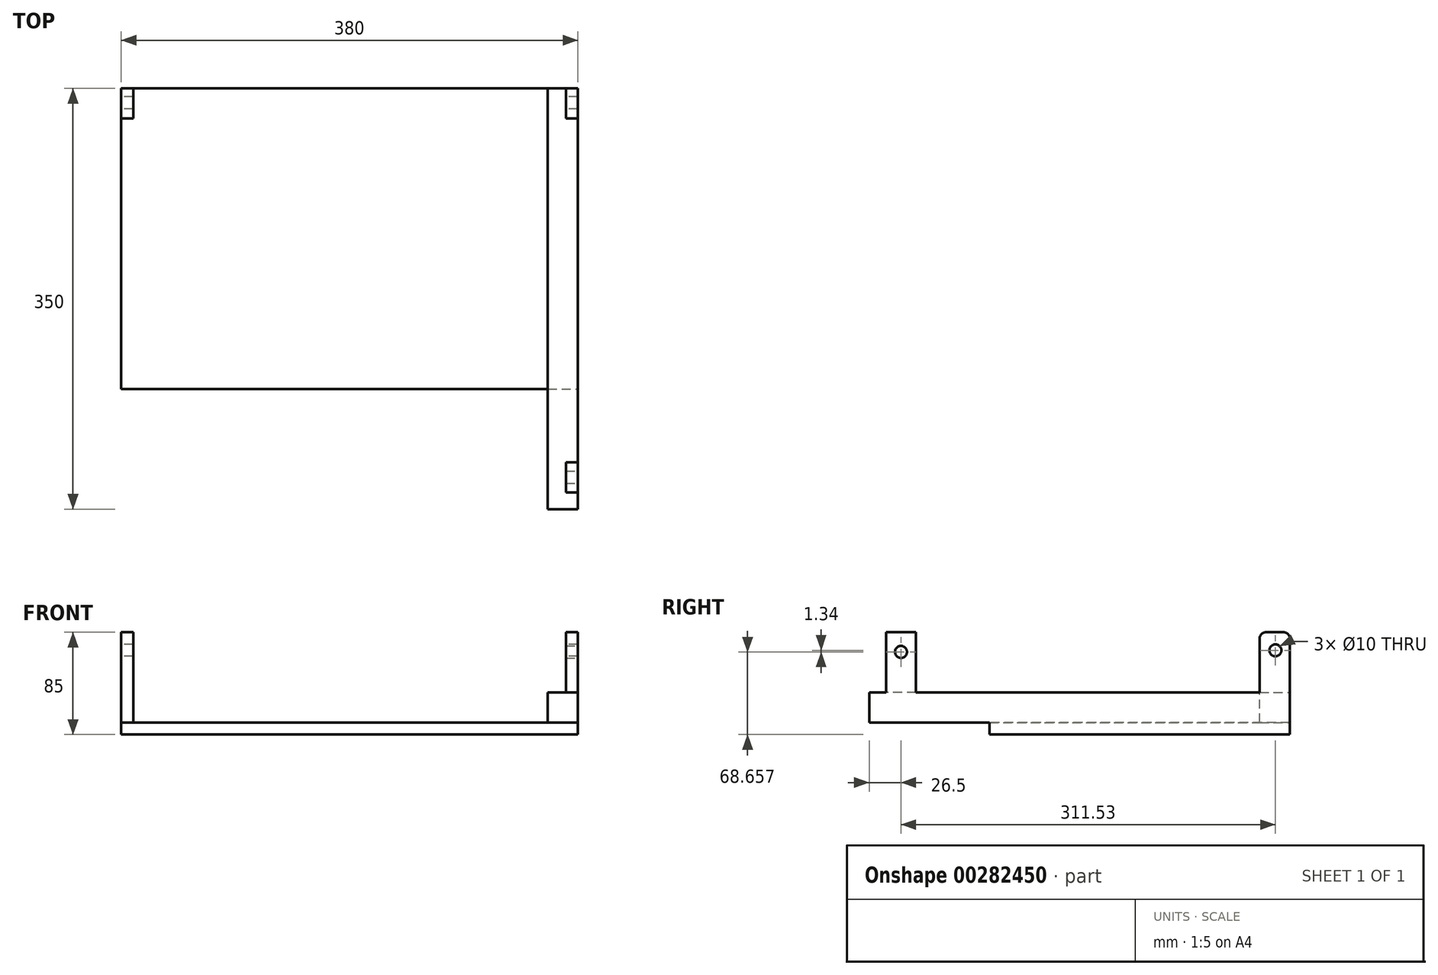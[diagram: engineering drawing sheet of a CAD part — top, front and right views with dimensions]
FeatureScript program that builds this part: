
annotation { "Feature Type Name" : "Feature", "Feature Type Description" : "" }
export const myFeature = defineFeature(function(context is Context, id is Id, definition is map)
    precondition{}
    {
        {
            var Q0;
            Q0=qCreatedBy(makeId("Front.planeOp"),FACE);
            var sketch = newSketch(context, id + "F0", { "sketchPlane" : qUnion([Q0])});
            skLineSegment(sketch, "E0.bottom", {"start": v(-278.94, 1.9) * mm, "end": v(101.06, 1.9) * mm});
            skLineSegment(sketch, "E0.top", {"start": v(-278.94, -8.1) * mm, "end": v(101.06, -8.1) * mm});
            skLineSegment(sketch, "E0.left", {"start": v(-278.94, 1.9) * mm, "end": v(-278.94, -8.1) * mm});
            skLineSegment(sketch, "E0.right", {"start": v(101.06, 1.9) * mm, "end": v(101.06, -8.1) * mm});
            skLineSegment(sketch, "E1.bottom", {"start": v(-278.94, 1.9) * mm, "end": v(-268.94, 1.9) * mm});
            skLineSegment(sketch, "E1.top", {"start": v(-278.94, 76.9) * mm, "end": v(-268.94, 76.9) * mm});
            skLineSegment(sketch, "E1.left", {"start": v(-278.94, 1.9) * mm, "end": v(-278.94, 76.9) * mm});
            skLineSegment(sketch, "E1.right", {"start": v(-268.94, 1.9) * mm, "end": v(-268.94, 76.9) * mm});
            skLineSegment(sketch, "E2.bottom", {"start": v(101.06, 1.9) * mm, "end": v(91.06, 1.9) * mm});
            skLineSegment(sketch, "E2.top", {"start": v(101.06, 76.9) * mm, "end": v(91.06, 76.9) * mm});
            skLineSegment(sketch, "E2.left", {"start": v(101.06, 1.9) * mm, "end": v(101.06, 76.9) * mm});
            skLineSegment(sketch, "E2.right", {"start": v(91.06, 1.9) * mm, "end": v(91.06, 76.9) * mm});
            skSolve(sketch);
        }
        {
            var Q0;
            Q0=makeQuery(id+"F0.imprint","IMPRINT",FACE,{"disambiguationData":[TD([[makeQuery(id+"F0.imprint","IMPRINT",EDGE,{"derivedFrom":sQuery(id+"F0.wireOp",EDGE,"E0.bottom")}),-1.0]])]});
            extrude(context, id + "F1", {"entities" : qUnion([Q0]), "depth" : 250 * mm});
        }
        {
            var Q0;
            Q0 = qSketchRegion(id + "F0", true);
            extrude(context, id + "F2", {"entities" : qUnion([Q0]), "operationType" : NewBodyOperationType.ADD, "depth" : 25 * mm});
        }
        {
            var Q0;
            {var subQ0=sQuery(id+"F0.wireOp",EDGE,"E0.left");Q0=makeQuery(id+"F2.boolean.opBoolean","MERGE",FACE,{"derivedFrom":[makeQuery(id+"F1.opExtrude","SWEPT_FACE",FACE,{"disambiguationData":[OSD([subQ0])]}),makeQuery(id+"F2.opExtrude","SWEPT_FACE",FACE,{"disambiguationData":[OSD([subQ0,sQuery(id+"F0.wireOp",EDGE,"E1.left")])]})]});}
            var sketch = newSketch(context, id + "F3", { "sketchPlane" : qUnion([Q0])});
            skCircle(sketch, "E3", {"center": v(11.97, 61.9) * mm, "radius": 5 * mm});
            skSolve(sketch);
        }
        {
            var Q0;
            Q0=makeQuery(id+"F3.imprint","IMPRINT",FACE,{"disambiguationData":[TD([[makeQuery(id+"F3.imprint","IMPRINT",EDGE,{"derivedFrom":sQuery(id+"F3.wireOp",EDGE,"E3")}),1.0]])]});
            extrude(context, id + "F4", {"entities" : qUnion([Q0]), "operationType" : NewBodyOperationType.REMOVE, "endBound" : BoundingType.THROUGH_ALL, "oppositeDirection" : true, "depth" : 25 * mm});
        }
        {
            var Q0;
            Q0=makeQuery(id+"F2.opExtrude","CAP_EDGE",EDGE,{"disambiguationData":[OSD([sQuery(id+"F0.wireOp",EDGE,"E1.top")])],"isStart":true});
            var Q1;
            Q1=makeQuery(id+"F2.opExtrude","CAP_EDGE",EDGE,{"disambiguationData":[OSD([sQuery(id+"F0.wireOp",EDGE,"E1.top")])],"isStart":false});
            var Q2;
            Q2=makeQuery(id+"F2.opExtrude","CAP_EDGE",EDGE,{"disambiguationData":[OSD([sQuery(id+"F0.wireOp",EDGE,"E2.top")])],"isStart":true});
            var Q3;
            Q3=makeQuery(id+"F2.opExtrude","CAP_EDGE",EDGE,{"disambiguationData":[OSD([sQuery(id+"F0.wireOp",EDGE,"E2.top")])],"isStart":false});
            fillet(context, id + "F5", {"entities" : qUnion([Q0, Q1, Q2, Q3]), "radius" : 5 * mm, "tangentPropagation" : true, "allowEdgeOverflow" : false});
        }
        {
            var Q0;
            Q0=makeQuery(id+"F1.opExtrude","SWEPT_FACE",FACE,{"disambiguationData":[OSD([sQuery(id+"F0.wireOp",EDGE,"E0.bottom"),sQuery(id+"F0.wireOp",EDGE,"E1.bottom"),sQuery(id+"F0.wireOp",EDGE,"E2.bottom")])]});
            var sketch = newSketch(context, id + "F6", { "sketchPlane" : qUnion([Q0])});
            skPoint(sketch, "E4.oppositeSnap0", {"position": v(101.06, -137.5) * mm});
            skLineSegment(sketch, "E4.bottom", {"start": v(76.06, 0) * mm, "end": v(101.06, 0) * mm});
            skLineSegment(sketch, "E4.top", {"start": v(76.06, -350) * mm, "end": v(101.06, -350) * mm});
            skLineSegment(sketch, "E4.left", {"start": v(76.06, 0) * mm, "end": v(76.06, -350) * mm});
            skLineSegment(sketch, "E4.right", {"start": v(101.06, 0) * mm, "end": v(101.06, -350) * mm});
            skSolve(sketch);
        }
        {
            var Q0;
            Q0 = qSketchRegion(id + "F6", true);
            extrude(context, id + "F7", {"entities" : qUnion([Q0]), "operationType" : NewBodyOperationType.ADD, "depth" : 25 * mm});
        }
        {
            var Q0;
            Q0=makeQuery(id+"F7.opExtrude","CAP_FACE",FACE,{"disambiguationData":[OSD([sQuery(id+"F6.wireOp",EDGE,"E4.bottom"),sQuery(id+"F6.wireOp",EDGE,"E4.top"),sQuery(id+"F6.wireOp",EDGE,"E4.left"),sQuery(id+"F6.wireOp",EDGE,"E4.right")])],"isStart":false});
            var sketch = newSketch(context, id + "F8", { "sketchPlane" : qUnion([Q0])});
            skLineSegment(sketch, "E5.bottom", {"start": v(101.06, -311) * mm, "end": v(91.06, -311) * mm});
            skLineSegment(sketch, "E5.top", {"start": v(101.06, -336) * mm, "end": v(91.06, -336) * mm});
            skLineSegment(sketch, "E5.left", {"start": v(101.06, -311) * mm, "end": v(101.06, -336) * mm});
            skLineSegment(sketch, "E5.right", {"start": v(91.06, -311) * mm, "end": v(91.06, -336) * mm});
            skSolve(sketch);
        }
        {
            var Q0;
            Q0=makeQuery(id+"F8.imprint","IMPRINT",FACE,{"disambiguationData":[TD([[makeQuery(id+"F8.imprint","IMPRINT",EDGE,{"derivedFrom":sQuery(id+"F8.wireOp",EDGE,"E5.bottom")}),1.0]])]});
            extrude(context, id + "F9", {"entities" : qUnion([Q0]), "operationType" : NewBodyOperationType.ADD, "depth" : 50 * mm});
        }
        {
            var Q0;
            {var subQ0=sQuery(id+"F0.wireOp",EDGE,"E0.right");Q0=makeQuery(id+"F9.boolean.opBoolean","MERGE",FACE,{"derivedFrom":[makeQuery(id+"F7.boolean.opBoolean","MERGE",FACE,{"derivedFrom":[makeQuery(id+"F2.boolean.opBoolean","MERGE",FACE,{"derivedFrom":[makeQuery(id+"F1.opExtrude","SWEPT_FACE",FACE,{"disambiguationData":[OSD([subQ0])]}),makeQuery(id+"F2.opExtrude","SWEPT_FACE",FACE,{"disambiguationData":[OSD([subQ0,sQuery(id+"F0.wireOp",EDGE,"E2.left")])]})]}),makeQuery(id+"F7.opExtrude","SWEPT_FACE",FACE,{"disambiguationData":[OSD([sQuery(id+"F6.wireOp",EDGE,"E4.right")])]})]}),makeQuery(id+"F9.opExtrude","SWEPT_FACE",FACE,{"disambiguationData":[OSD([sQuery(id+"F8.wireOp",EDGE,"E5.left")])]})]});}
            var sketch = newSketch(context, id + "F10", { "sketchPlane" : qUnion([Q0])});
            skCircle(sketch, "E6", {"center": v(-323.5, 60.57) * mm, "radius": 5 * mm});
            skPoint(sketch, "E6.centerSnap0", {"position": v(-323.5, 76.9) * mm});
            skSolve(sketch);
        }
        {
            var Q0;
            Q0=makeQuery(id+"F10.imprint","IMPRINT",FACE,{"disambiguationData":[TD([[makeQuery(id+"F10.imprint","IMPRINT",EDGE,{"derivedFrom":sQuery(id+"F10.wireOp",EDGE,"E6")}),1.0]])]});
            extrude(context, id + "F11", {"entities" : qUnion([Q0]), "operationType" : NewBodyOperationType.REMOVE, "endBound" : BoundingType.THROUGH_ALL, "oppositeDirection" : true, "depth" : 25 * mm});
        }
    });
